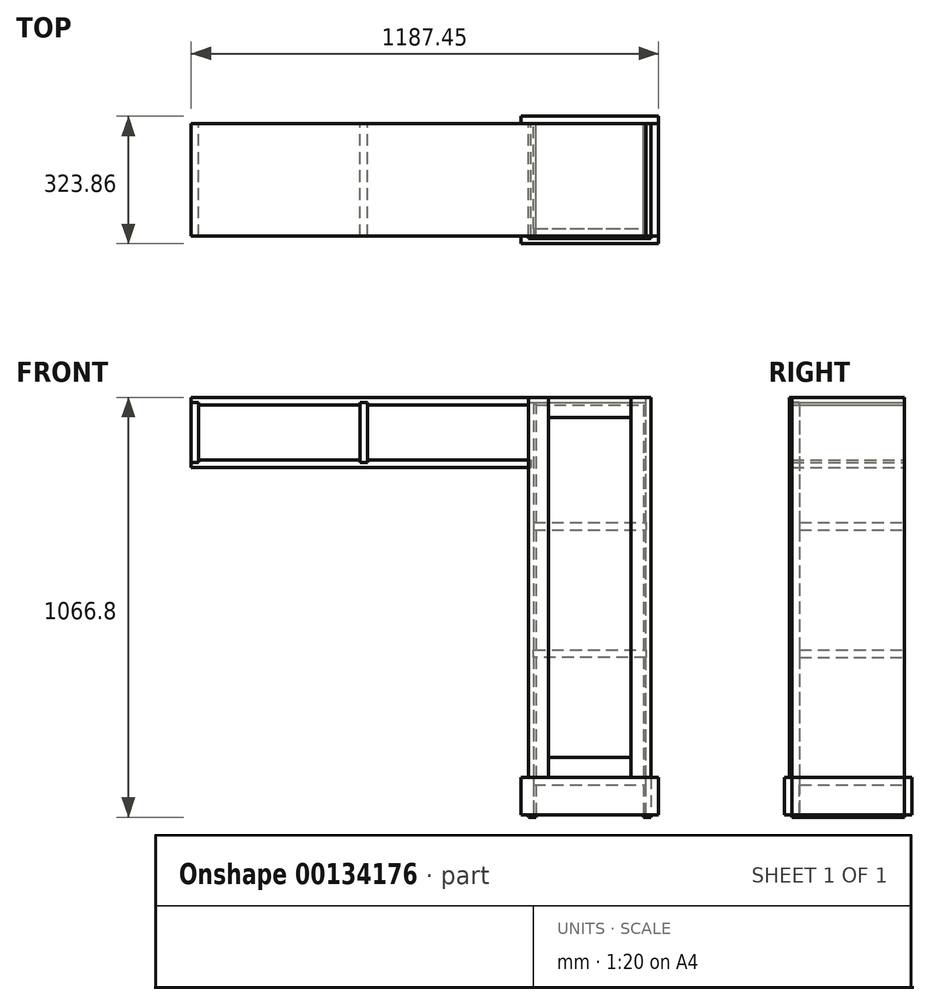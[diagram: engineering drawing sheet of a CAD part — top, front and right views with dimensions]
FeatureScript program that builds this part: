
annotation { "Feature Type Name" : "Feature", "Feature Type Description" : "" }
export const myFeature = defineFeature(function(context is Context, id is Id, definition is map)
    precondition{}
    {
        {
            var Q0;
            Q0=qCreatedBy(makeId("Front.planeOp"),FACE);
            var sketch = newSketch(context, id + "F0", { "sketchPlane" : qUnion([Q0])});
            skLineSegment(sketch, "E0.left", {"start": v(0, 908.05) * mm, "end": v(0, 1047.75) * mm});
            skLineSegment(sketch, "E0.right", {"start": v(19.05, 908.05) * mm, "end": v(19.05, 1047.75) * mm});
            skLineSegment(sketch, "E1.top", {"start": v(0, 889) * mm, "end": v(857.25, 889) * mm});
            skLineSegment(sketch, "E1.left", {"start": v(0, 908.05) * mm, "end": v(0, 889) * mm});
            skLineSegment(sketch, "E2.top", {"start": v(0, 1066.8) * mm, "end": v(1168.4, 1066.8) * mm});
            skLineSegment(sketch, "E2.left", {"start": v(0, 1047.75) * mm, "end": v(0, 1066.8) * mm});
            skLineSegment(sketch, "E2.right", {"start": v(1168.4, 1047.75) * mm, "end": v(1168.4, 1066.8) * mm});
            skLineSegment(sketch, "E3.top", {"start": v(857.25, 0) * mm, "end": v(876.3, 0) * mm});
            skLineSegment(sketch, "E3.left", {"start": v(857.25, 1047.75) * mm, "end": v(857.25, 908.05) * mm});
            skLineSegment(sketch, "E3.right", {"start": v(876.3, 1047.75) * mm, "end": v(876.3, 749.3) * mm});
            skLineSegment(sketch, "E4.top", {"start": v(1168.4, 0) * mm, "end": v(1149.35, 0) * mm});
            skLineSegment(sketch, "E4.left", {"start": v(1168.4, 1047.75) * mm, "end": v(1168.4, 0) * mm});
            skLineSegment(sketch, "E4.right", {"start": v(1149.35, 1047.75) * mm, "end": v(1149.35, 749.3) * mm});
            skLineSegment(sketch, "E5.bottom", {"start": v(876.3, 425.45) * mm, "end": v(1149.35, 425.45) * mm});
            skLineSegment(sketch, "E5.top", {"start": v(876.3, 406.4) * mm, "end": v(1149.35, 406.4) * mm});
            skLineSegment(sketch, "E6.top", {"start": v(857.25, 101.6) * mm, "end": v(838.2, 101.6) * mm});
            skLineSegment(sketch, "E6.left", {"start": v(857.25, 6.35) * mm, "end": v(857.25, 101.6) * mm});
            skLineSegment(sketch, "E7.bottom", {"start": v(1168.4, 6.35) * mm, "end": v(1187.45, 6.35) * mm});
            skLineSegment(sketch, "E7.top", {"start": v(1168.4, 101.6) * mm, "end": v(1187.45, 101.6) * mm});
            skLineSegment(sketch, "E7.left", {"start": v(1168.4, 6.35) * mm, "end": v(1168.4, 101.6) * mm});
            skLineSegment(sketch, "E8.bottom", {"start": v(838.2, 101.6) * mm, "end": v(857.25, 101.6) * mm});
            skLineSegment(sketch, "E8.left", {"start": v(838.2, 101.6) * mm, "end": v(838.2, 6.35) * mm});
            skLineSegment(sketch, "E8.right", {"start": v(1187.45, 101.6) * mm, "end": v(1187.45, 6.35) * mm});
            skLineSegment(sketch, "E9.bottom", {"start": v(876.3, 749.3) * mm, "end": v(1149.35, 749.3) * mm});
            skLineSegment(sketch, "E9.top", {"start": v(869.95, 730.25) * mm, "end": v(1149.35, 730.25) * mm});
            skLineSegment(sketch, "E10.bottom", {"start": v(876.3, 101.6) * mm, "end": v(1149.35, 101.6) * mm});
            skLineSegment(sketch, "E10.top", {"start": v(876.3, 82.55) * mm, "end": v(1149.35, 82.55) * mm});
            skLineSegment(sketch, "E11.bottom", {"start": v(876.3, 749.3) * mm, "end": v(869.95, 749.3) * mm});
            skLineSegment(sketch, "E11.top", {"start": v(876.3, 730.25) * mm, "end": v(869.95, 730.25) * mm});
            skLineSegment(sketch, "E11.right", {"start": v(869.95, 749.3) * mm, "end": v(869.95, 730.25) * mm});
            skLineSegment(sketch, "E12.bottom", {"start": v(1149.35, 749.3) * mm, "end": v(1155.7, 749.3) * mm});
            skLineSegment(sketch, "E12.top", {"start": v(1149.35, 730.25) * mm, "end": v(1155.7, 730.25) * mm});
            skLineSegment(sketch, "E12.right", {"start": v(1155.7, 749.3) * mm, "end": v(1155.7, 730.25) * mm});
            skLineSegment(sketch, "E13.trimOffspring", {"start": v(1149.35, 730.25) * mm, "end": v(1149.35, 425.45) * mm});
            skLineSegment(sketch, "E14.trimOffspring", {"start": v(876.3, 730.25) * mm, "end": v(876.3, 425.45) * mm});
            skLineSegment(sketch, "E15.trimOffspring", {"start": v(19.05, 908.05) * mm, "end": v(428.63, 908.05) * mm});
            skLineSegment(sketch, "E16.trimOffspring", {"start": v(19.05, 1047.75) * mm, "end": v(428.63, 1047.75) * mm});
            skLineSegment(sketch, "E17", {"start": v(19.05, 901.7) * mm, "end": v(0, 901.7) * mm});
            skLineSegment(sketch, "E18", {"start": v(19.05, 1054.1) * mm, "end": v(0, 1054.1) * mm});
            skLineSegment(sketch, "E19", {"start": v(19.05, 1047.75) * mm, "end": v(19.05, 1054.1) * mm});
            skLineSegment(sketch, "E20", {"start": v(19.05, 901.7) * mm, "end": v(19.05, 908.05) * mm});
            skLineSegment(sketch, "E21", {"start": v(428.63, 1054.1) * mm, "end": v(447.68, 1054.1) * mm});
            skLineSegment(sketch, "E22", {"start": v(447.68, 1047.75) * mm, "end": v(447.68, 901.7) * mm});
            skLineSegment(sketch, "E23", {"start": v(447.68, 901.7) * mm, "end": v(428.63, 901.7) * mm});
            skLineSegment(sketch, "E24", {"start": v(428.63, 901.7) * mm, "end": v(428.63, 1054.1) * mm});
            skLineSegment(sketch, "E25.trimOffspring", {"start": v(447.68, 1047.75) * mm, "end": v(857.25, 1047.75) * mm});
            skLineSegment(sketch, "E26.trimOffspring", {"start": v(447.68, 908.05) * mm, "end": v(857.25, 908.05) * mm});
            skLineSegment(sketch, "E27", {"start": v(857.25, 1054.1) * mm, "end": v(876.3, 1054.1) * mm});
            skLineSegment(sketch, "E28", {"start": v(857.25, 1054.1) * mm, "end": v(857.25, 1047.75) * mm});
            skLineSegment(sketch, "E29", {"start": v(857.25, 908.05) * mm, "end": v(863.6, 908.05) * mm});
            skLineSegment(sketch, "E30", {"start": v(863.6, 908.05) * mm, "end": v(863.6, 889) * mm});
            skLineSegment(sketch, "E31", {"start": v(863.6, 889) * mm, "end": v(857.25, 889) * mm});
            skLineSegment(sketch, "E32", {"start": v(1149.35, 1047.75) * mm, "end": v(1155.7, 1047.75) * mm});
            skLineSegment(sketch, "E33", {"start": v(876.3, 406.4) * mm, "end": v(869.95, 406.4) * mm});
            skLineSegment(sketch, "E34", {"start": v(869.95, 406.4) * mm, "end": v(869.95, 425.45) * mm});
            skLineSegment(sketch, "E35", {"start": v(869.95, 425.45) * mm, "end": v(1155.7, 425.45) * mm});
            skLineSegment(sketch, "E36", {"start": v(1155.7, 425.45) * mm, "end": v(1155.7, 406.4) * mm});
            skLineSegment(sketch, "E37", {"start": v(1155.7, 406.4) * mm, "end": v(1149.35, 406.4) * mm});
            skLineSegment(sketch, "E38.trimOffspring", {"start": v(1149.35, 406.4) * mm, "end": v(1149.35, 101.6) * mm});
            skLineSegment(sketch, "E39.trimOffspring", {"start": v(876.3, 406.4) * mm, "end": v(876.3, 101.6) * mm});
            skLineSegment(sketch, "E40", {"start": v(1149.35, 82.55) * mm, "end": v(1155.7, 82.55) * mm});
            skLineSegment(sketch, "E41", {"start": v(1155.7, 82.55) * mm, "end": v(1155.7, 101.6) * mm});
            skLineSegment(sketch, "E42", {"start": v(1155.7, 101.6) * mm, "end": v(869.95, 101.6) * mm});
            skLineSegment(sketch, "E43", {"start": v(869.95, 101.6) * mm, "end": v(869.95, 82.55) * mm});
            skLineSegment(sketch, "E44", {"start": v(869.95, 82.55) * mm, "end": v(876.3, 82.55) * mm});
            skLineSegment(sketch, "E45.trimOffspring", {"start": v(876.3, 82.55) * mm, "end": v(876.3, 0) * mm});
            skLineSegment(sketch, "E46.trimOffspring", {"start": v(1149.35, 82.55) * mm, "end": v(1149.35, 0) * mm});
            skLineSegment(sketch, "E47.trimOffspring", {"start": v(857.25, 889) * mm, "end": v(857.25, 0) * mm});
            skLineSegment(sketch, "E48.trimOffspring", {"start": v(876.3, 1047.75) * mm, "end": v(1149.35, 1047.75) * mm});
            skLineSegment(sketch, "E49", {"start": v(876.3, 1047.75) * mm, "end": v(876.3, 1054.1) * mm});
            skLineSegment(sketch, "E50.trimOffspring", {"start": v(869.95, 101.6) * mm, "end": v(1155.7, 101.6) * mm});
            skLineSegment(sketch, "E51", {"start": v(1155.7, 1047.75) * mm, "end": v(1155.7, 1066.8) * mm});
            skLineSegment(sketch, "E52", {"start": v(838.2, 6.35) * mm, "end": v(857.25, 6.35) * mm});
            skLineSegment(sketch, "E53", {"start": v(876.3, 0) * mm, "end": v(1149.35, 0) * mm});
            skLineSegment(sketch, "E54", {"start": v(447.68, 1054.1) * mm, "end": v(447.68, 1047.75) * mm});
            skSolve(sketch);
        }
        {
            var Q0;
            {var subQ0=sQuery(id+"F0.wireOp",EDGE,"E8.bottom");Q0=makeQuery(id+"F0.imprint","IMPRINT",FACE,{"disambiguationData":[TD([[makeQuery(id+"F0.imprint","IMPRINT",EDGE,{"derivedFrom":subQ0}),-1.0]])]});}
            var Q1;
            Q1=makeQuery(id+"F0.imprint","IMPRINT",FACE,{"disambiguationData":[TD([[makeQuery(id+"F0.imprint","IMPRINT",EDGE,{"derivedFrom":sQuery(id+"F0.wireOp",EDGE,"E10.top")}),1.0]])]});
            var Q2;
            Q2=makeQuery(id+"F0.imprint","IMPRINT",FACE,{"disambiguationData":[TD([[makeQuery(id+"F0.imprint","IMPRINT",EDGE,{"derivedFrom":sQuery(id+"F0.wireOp",EDGE,"E7.bottom")}),1.0]])]});
            var Q3;
            Q3=makeQuery(id+"F0.imprint","IMPRINT",FACE,{"disambiguationData":[TD([[makeQuery(id+"F0.imprint","IMPRINT",EDGE,{"derivedFrom":sQuery(id+"F0.wireOp",EDGE,"E5.top")}),1.0]])]});
            var Q4;
            Q4=makeQuery(id+"F0.imprint","IMPRINT",FACE,{"disambiguationData":[TD([[makeQuery(id+"F0.imprint","IMPRINT",EDGE,{"derivedFrom":sQuery(id+"F0.wireOp",EDGE,"E9.bottom")}),-1.0]])]});
            var Q5;
            {var subQ6=sQuery(id+"F0.wireOp",EDGE,"E16.trimOffspring");Q5=makeQuery(id+"F0.imprint","IMPRINT",FACE,{"disambiguationData":[TD([[makeQuery(id+"F0.imprint","IMPRINT",EDGE,{"derivedFrom":subQ6}),1.0]])]});}
            var Q6;
            {var subQ4=sQuery(id+"F0.wireOp",EDGE,"E1.top");Q6=makeQuery(id+"F0.imprint","IMPRINT",FACE,{"disambiguationData":[TD([[makeQuery(id+"F0.imprint","IMPRINT",EDGE,{"derivedFrom":subQ4}),1.0]])]});}
            extrude(context, id + "F1", {"entities" : qUnion([Q0, Q1, Q2, Q3, Q4, Q5, Q6]), "endBound" : BoundingType.SYMMETRIC, "depth" : 285.75 * mm});
        }
        {
            var Q0;
            {var subQ9=sQuery(id+"F0.wireOp",EDGE,"E3.top");Q0=makeQuery(id+"F0.imprint","IMPRINT",FACE,{"disambiguationData":[TD([[makeQuery(id+"F0.imprint","IMPRINT",EDGE,{"derivedFrom":subQ9}),1.0]])]});}
            var Q1;
            {var subQ1=sQuery(id+"F0.wireOp",EDGE,"E2.right");Q1=makeQuery(id+"F0.imprint","IMPRINT",FACE,{"disambiguationData":[TD([[makeQuery(id+"F0.imprint","IMPRINT",EDGE,{"derivedFrom":subQ1}),1.0]])]});}
            var Q2;
            {var subQ4=sQuery(id+"F0.wireOp",EDGE,"E21");Q2=makeQuery(id+"F0.imprint","IMPRINT",FACE,{"disambiguationData":[TD([[makeQuery(id+"F0.imprint","IMPRINT",EDGE,{"derivedFrom":subQ4}),-1.0]])]});}
            var Q3;
            {var subQ1=sQuery(id+"F0.wireOp",EDGE,"E0.left");Q3=makeQuery(id+"F0.imprint","IMPRINT",FACE,{"disambiguationData":[TD([[makeQuery(id+"F0.imprint","IMPRINT",EDGE,{"derivedFrom":subQ1}),-1.0]])]});}
            var Q4;
            Q4=makeQuery(id+"F1.opExtrude","CAP_FACE",FACE,{"disambiguationData":[OSD([sQuery(id+"F0.wireOp",EDGE,"E2.top"),sQuery(id+"F0.wireOp",EDGE,"E2.left"),sQuery(id+"F0.wireOp",EDGE,"E16.trimOffspring"),sQuery(id+"F0.wireOp",EDGE,"E18"),sQuery(id+"F0.wireOp",EDGE,"E19"),sQuery(id+"F0.wireOp",EDGE,"E21"),sQuery(id+"F0.wireOp",EDGE,"E24"),sQuery(id+"F0.wireOp",EDGE,"E25.trimOffspring"),sQuery(id+"F0.wireOp",EDGE,"E27"),sQuery(id+"F0.wireOp",EDGE,"E28"),sQuery(id+"F0.wireOp",EDGE,"E32"),sQuery(id+"F0.wireOp",EDGE,"E48.trimOffspring"),sQuery(id+"F0.wireOp",EDGE,"E49"),sQuery(id+"F0.wireOp",EDGE,"E51"),sQuery(id+"F0.wireOp",EDGE,"E54")])],"isStart":false});
            var Q5;
            Q5=makeQuery(id+"F1.opExtrude","CAP_FACE",FACE,{"disambiguationData":[OSD([sQuery(id+"F0.wireOp",EDGE,"E2.top"),sQuery(id+"F0.wireOp",EDGE,"E2.left"),sQuery(id+"F0.wireOp",EDGE,"E16.trimOffspring"),sQuery(id+"F0.wireOp",EDGE,"E18"),sQuery(id+"F0.wireOp",EDGE,"E19"),sQuery(id+"F0.wireOp",EDGE,"E21"),sQuery(id+"F0.wireOp",EDGE,"E24"),sQuery(id+"F0.wireOp",EDGE,"E25.trimOffspring"),sQuery(id+"F0.wireOp",EDGE,"E27"),sQuery(id+"F0.wireOp",EDGE,"E28"),sQuery(id+"F0.wireOp",EDGE,"E32"),sQuery(id+"F0.wireOp",EDGE,"E48.trimOffspring"),sQuery(id+"F0.wireOp",EDGE,"E49"),sQuery(id+"F0.wireOp",EDGE,"E51"),sQuery(id+"F0.wireOp",EDGE,"E54")])],"isStart":true});
            extrude(context, id + "F2", {"entities" : qUnion([Q0, Q1, Q2, Q3]), "endBound" : BoundingType.UP_TO_SURFACE, "endBoundEntityFace" : qUnion([Q4]), "depth" : 25.4 * mm, "hasSecondDirection" : true, "secondDirectionBound" : SecondDirectionBoundingType.UP_TO_SURFACE, "secondDirectionOppositeDirection" : true, "secondDirectionBoundEntityFace" : qUnion([Q5]), "secondDirectionDepth" : 25.4 * mm});
        }
        {
            var Q0;
            Q0=makeQuery(id+"F1.opExtrude","CAP_FACE",FACE,{"disambiguationData":[OSD([sQuery(id+"F0.wireOp",EDGE,"E2.top"),sQuery(id+"F0.wireOp",EDGE,"E2.left"),sQuery(id+"F0.wireOp",EDGE,"E16.trimOffspring"),sQuery(id+"F0.wireOp",EDGE,"E18"),sQuery(id+"F0.wireOp",EDGE,"E19"),sQuery(id+"F0.wireOp",EDGE,"E21"),sQuery(id+"F0.wireOp",EDGE,"E24"),sQuery(id+"F0.wireOp",EDGE,"E25.trimOffspring"),sQuery(id+"F0.wireOp",EDGE,"E27"),sQuery(id+"F0.wireOp",EDGE,"E28"),sQuery(id+"F0.wireOp",EDGE,"E32"),sQuery(id+"F0.wireOp",EDGE,"E48.trimOffspring"),sQuery(id+"F0.wireOp",EDGE,"E49"),sQuery(id+"F0.wireOp",EDGE,"E51"),sQuery(id+"F0.wireOp",EDGE,"E54")])],"isStart":false});
            var sketch = newSketch(context, id + "F3", { "sketchPlane" : qUnion([Q0])});
            skLineSegment(sketch, "E55.bottom", {"start": v(838.2, 101.6) * mm, "end": v(1187.45, 101.6) * mm});
            skLineSegment(sketch, "E55.top", {"start": v(838.2, 6.35) * mm, "end": v(1187.45, 6.35) * mm});
            skLineSegment(sketch, "E55.left", {"start": v(838.2, 101.6) * mm, "end": v(838.2, 6.35) * mm});
            skLineSegment(sketch, "E55.right", {"start": v(1187.45, 101.6) * mm, "end": v(1187.45, 6.35) * mm});
            skSolve(sketch);
        }
        {
            var Q0;
            Q0 = qSketchRegion(id + "F3", true);
            extrude(context, id + "F4", {"entities" : qUnion([Q0]), "depth" : 19.05 * mm});
        }
        {
            var Q0;
            Q0=makeQuery(id+"F1.opExtrude","CAP_FACE",FACE,{"disambiguationData":[OSD([sQuery(id+"F0.wireOp",EDGE,"E2.top"),sQuery(id+"F0.wireOp",EDGE,"E2.left"),sQuery(id+"F0.wireOp",EDGE,"E16.trimOffspring"),sQuery(id+"F0.wireOp",EDGE,"E18"),sQuery(id+"F0.wireOp",EDGE,"E19"),sQuery(id+"F0.wireOp",EDGE,"E21"),sQuery(id+"F0.wireOp",EDGE,"E24"),sQuery(id+"F0.wireOp",EDGE,"E25.trimOffspring"),sQuery(id+"F0.wireOp",EDGE,"E27"),sQuery(id+"F0.wireOp",EDGE,"E28"),sQuery(id+"F0.wireOp",EDGE,"E32"),sQuery(id+"F0.wireOp",EDGE,"E48.trimOffspring"),sQuery(id+"F0.wireOp",EDGE,"E49"),sQuery(id+"F0.wireOp",EDGE,"E51"),sQuery(id+"F0.wireOp",EDGE,"E54")])],"isStart":true});
            var sketch = newSketch(context, id + "F5", { "sketchPlane" : qUnion([Q0])});
            skLineSegment(sketch, "E56.bottom", {"start": v(-838.2, 101.6) * mm, "end": v(-838.2, 101.6) * mm});
            skLineSegment(sketch, "E56.top", {"start": v(-838.2, 101.6) * mm, "end": v(-838.2, 101.6) * mm});
            skLineSegment(sketch, "E56.left", {"start": v(-838.2, 101.6) * mm, "end": v(-838.2, 101.6) * mm});
            skLineSegment(sketch, "E56.right", {"start": v(-838.2, 101.6) * mm, "end": v(-838.2, 101.6) * mm});
            skLineSegment(sketch, "E57.bottom", {"start": v(-838.2, 101.6) * mm, "end": v(-1187.45, 101.6) * mm});
            skLineSegment(sketch, "E57.top", {"start": v(-838.2, 6.35) * mm, "end": v(-1187.45, 6.35) * mm});
            skLineSegment(sketch, "E57.left", {"start": v(-838.2, 101.6) * mm, "end": v(-838.2, 6.35) * mm});
            skLineSegment(sketch, "E57.right", {"start": v(-1187.45, 101.6) * mm, "end": v(-1187.45, 6.35) * mm});
            skSolve(sketch);
        }
        {
            var Q0;
            Q0 = qSketchRegion(id + "F5", true);
            extrude(context, id + "F6", {"entities" : qUnion([Q0]), "depth" : 19.05 * mm});
        }
        {
            var Q0;
            Q0=makeQuery(id+"F2.opExtrude","SWEPT_FACE",FACE,{"disambiguationData":[OSD([sQuery(id+"F0.wireOp",EDGE,"E2.top")])]});
            var sketch = newSketch(context, id + "F7", { "sketchPlane" : qUnion([Q0])});
            skLineSegment(sketch, "E58.bottom", {"start": v(0, 190.5) * mm, "end": v(1155.7, 190.5) * mm});
            skLineSegment(sketch, "E58.top", {"start": v(63.5, -190.5) * mm, "end": v(1155.7, -190.5) * mm});
            skLineSegment(sketch, "E58.left", {"start": v(0, 190.5) * mm, "end": v(0, -127) * mm});
            skLineSegment(sketch, "E58.right", {"start": v(1219.2, 127) * mm, "end": v(1219.2, -127) * mm});
            skPoint(sketch, "E59.visualSharp", {"position": v(1219.2, 190.5) * mm});
            skArc(sketch, "E59.filletArc", {"start": v(1219.2, 127) * mm, "mid": v(1200.6, 171.9) * mm, "end": v(1155.7, 190.5) * mm});
            skPoint(sketch, "E60.visualSharp", {"position": v(1219.2, -190.5) * mm});
            skArc(sketch, "E60.filletArc", {"start": v(1155.7, -190.5) * mm, "mid": v(1200.6, -171.9) * mm, "end": v(1219.2, -127) * mm});
            skPoint(sketch, "E61.visualSharp", {"position": v(0, -190.5) * mm});
            skArc(sketch, "E61.filletArc", {"start": v(0, -127) * mm, "mid": v(18.6, -171.9) * mm, "end": v(63.5, -190.5) * mm});
            skSolve(sketch);
        }
        {
            var Q0;
            Q0=makeQuery(id+"F1.opExtrude","CAP_FACE",FACE,{"disambiguationData":[OSD([sQuery(id+"F0.wireOp",EDGE,"E2.top"),sQuery(id+"F0.wireOp",EDGE,"E2.left"),sQuery(id+"F0.wireOp",EDGE,"E16.trimOffspring"),sQuery(id+"F0.wireOp",EDGE,"E18"),sQuery(id+"F0.wireOp",EDGE,"E19"),sQuery(id+"F0.wireOp",EDGE,"E21"),sQuery(id+"F0.wireOp",EDGE,"E24"),sQuery(id+"F0.wireOp",EDGE,"E25.trimOffspring"),sQuery(id+"F0.wireOp",EDGE,"E27"),sQuery(id+"F0.wireOp",EDGE,"E28"),sQuery(id+"F0.wireOp",EDGE,"E32"),sQuery(id+"F0.wireOp",EDGE,"E48.trimOffspring"),sQuery(id+"F0.wireOp",EDGE,"E49"),sQuery(id+"F0.wireOp",EDGE,"E51"),sQuery(id+"F0.wireOp",EDGE,"E54")])],"isStart":false});
            var sketch = newSketch(context, id + "F8", { "sketchPlane" : qUnion([Q0])});
            skLineSegment(sketch, "E62.bottom", {"start": v(869.95, 1054.1) * mm, "end": v(1155.7, 1054.1) * mm});
            skLineSegment(sketch, "E62.top", {"start": v(869.95, 6.35) * mm, "end": v(1155.7, 6.35) * mm});
            skLineSegment(sketch, "E62.left", {"start": v(869.95, 1054.1) * mm, "end": v(869.95, 6.35) * mm});
            skLineSegment(sketch, "E62.right", {"start": v(1155.7, 1054.1) * mm, "end": v(1155.7, 6.35) * mm});
            skSolve(sketch);
        }
        {
            var Q0;
            Q0 = qSketchRegion(id + "F8", true);
            extrude(context, id + "F9", {"entities" : qUnion([Q0]), "operationType" : NewBodyOperationType.REMOVE, "oppositeDirection" : true, "depth" : 19.05 * mm});
        }
        {
            var Q0;
            Q0 = qSketchRegion(id + "F8", true);
            extrude(context, id + "F10", {"entities" : qUnion([Q0]), "oppositeDirection" : true, "depth" : 19.05 * mm});
        }
        {
            var Q0;
            Q0=makeQuery(id+"F1.opExtrude","CAP_FACE",FACE,{"disambiguationData":[OSD([sQuery(id+"F0.wireOp",EDGE,"E2.top"),sQuery(id+"F0.wireOp",EDGE,"E2.left"),sQuery(id+"F0.wireOp",EDGE,"E16.trimOffspring"),sQuery(id+"F0.wireOp",EDGE,"E18"),sQuery(id+"F0.wireOp",EDGE,"E19"),sQuery(id+"F0.wireOp",EDGE,"E21"),sQuery(id+"F0.wireOp",EDGE,"E24"),sQuery(id+"F0.wireOp",EDGE,"E25.trimOffspring"),sQuery(id+"F0.wireOp",EDGE,"E27"),sQuery(id+"F0.wireOp",EDGE,"E28"),sQuery(id+"F0.wireOp",EDGE,"E32"),sQuery(id+"F0.wireOp",EDGE,"E48.trimOffspring"),sQuery(id+"F0.wireOp",EDGE,"E49"),sQuery(id+"F0.wireOp",EDGE,"E51"),sQuery(id+"F0.wireOp",EDGE,"E54")])],"isStart":false});
            var sketch = newSketch(context, id + "F11", { "sketchPlane" : qUnion([Q0])});
            skLineSegment(sketch, "E63.bottom", {"start": v(857.25, 1066.8) * mm, "end": v(908.05, 1066.8) * mm});
            skLineSegment(sketch, "E63.top", {"start": v(857.25, 101.6) * mm, "end": v(908.05, 101.6) * mm});
            skLineSegment(sketch, "E63.left", {"start": v(857.25, 1066.8) * mm, "end": v(857.25, 101.6) * mm});
            skLineSegment(sketch, "E63.right", {"start": v(908.05, 1066.8) * mm, "end": v(908.05, 101.6) * mm});
            skLineSegment(sketch, "E64.bottom", {"start": v(1168.4, 1066.8) * mm, "end": v(1117.6, 1066.8) * mm});
            skLineSegment(sketch, "E64.top", {"start": v(1168.4, 101.6) * mm, "end": v(1117.6, 101.6) * mm});
            skLineSegment(sketch, "E64.left", {"start": v(1168.4, 1066.8) * mm, "end": v(1168.4, 101.6) * mm});
            skLineSegment(sketch, "E64.right", {"start": v(1117.6, 1066.8) * mm, "end": v(1117.6, 101.6) * mm});
            skLineSegment(sketch, "E65.bottom", {"start": v(908.05, 1066.8) * mm, "end": v(1117.6, 1066.8) * mm});
            skLineSegment(sketch, "E65.top", {"start": v(908.05, 1016) * mm, "end": v(908.05, 1016) * mm});
            skLineSegment(sketch, "E65.left", {"start": v(908.05, 1066.8) * mm, "end": v(908.05, 1016) * mm});
            skLineSegment(sketch, "E65.right", {"start": v(1117.6, 1066.8) * mm, "end": v(1117.6, 1016) * mm});
            skLineSegment(sketch, "E66.bottom", {"start": v(908.05, 101.6) * mm, "end": v(1117.6, 101.6) * mm});
            skLineSegment(sketch, "E66.top", {"start": v(908.05, 152.4) * mm, "end": v(908.05, 152.4) * mm});
            skLineSegment(sketch, "E66.left", {"start": v(908.05, 101.6) * mm, "end": v(908.05, 152.4) * mm});
            skLineSegment(sketch, "E66.right", {"start": v(1117.6, 101.6) * mm, "end": v(1117.6, 152.4) * mm});
            skLineSegment(sketch, "E67", {"start": v(1117.6, 152.4) * mm, "end": v(1117.6, 152.4) * mm});
            skLineSegment(sketch, "E68", {"start": v(908.05, 152.4) * mm, "end": v(1117.6, 152.4) * mm});
            skLineSegment(sketch, "E69", {"start": v(908.05, 1016) * mm, "end": v(1117.6, 1016) * mm});
            skLineSegment(sketch, "E70", {"start": v(1117.6, 1016) * mm, "end": v(1117.6, 1016) * mm});
            skSolve(sketch);
        }
        {
            var Q0;
            Q0=makeQuery(id+"F11.imprint","IMPRINT",FACE,{"disambiguationData":[TD([[makeQuery(id+"F11.imprint","IMPRINT",EDGE,{"derivedFrom":sQuery(id+"F11.wireOp",EDGE,"E66.bottom")}),1.0]])]});
            var Q1;
            {var subQ0=sQuery(id+"F11.wireOp",EDGE,"E65.bottom");Q1=makeQuery(id+"F11.imprint","IMPRINT",FACE,{"disambiguationData":[TD([[makeQuery(id+"F11.imprint","IMPRINT",EDGE,{"derivedFrom":subQ0}),-1.0]])]});}
            var Q2;
            {var subQ0=sQuery(id+"F11.wireOp",EDGE,"E69");Q2=makeQuery(id+"F11.imprint","IMPRINT",FACE,{"disambiguationData":[TD([[makeQuery(id+"F11.imprint","IMPRINT",EDGE,{"derivedFrom":subQ0}),1.0]])]});}
            extrude(context, id + "F12", {"entities" : qUnion([Q0, Q1, Q2]), "depth" : 6.35 * mm});
        }
        {
            var Q0;
            Q0=makeQuery(id+"F11.imprint","IMPRINT",FACE,{"disambiguationData":[TD([[makeQuery(id+"F11.imprint","IMPRINT",EDGE,{"derivedFrom":sQuery(id+"F11.wireOp",EDGE,"E63.bottom")}),-1.0]])]});
            var Q1;
            Q1=makeQuery(id+"F11.imprint","IMPRINT",FACE,{"disambiguationData":[TD([[makeQuery(id+"F11.imprint","IMPRINT",EDGE,{"derivedFrom":sQuery(id+"F11.wireOp",EDGE,"E64.bottom")}),-1.0]])]});
            var Q2;
            {var subQ7=sQuery(id+"F11.wireOp",EDGE,"E63.top");Q2=makeQuery(id+"F11.imprint","IMPRINT",FACE,{"disambiguationData":[TD([[makeQuery(id+"F11.imprint","IMPRINT",EDGE,{"derivedFrom":subQ7}),1.0]])]});}
            var Q3;
            Q3=makeQuery(id+"F11.imprint","IMPRINT",FACE,{"disambiguationData":[TD([[makeQuery(id+"F11.imprint","IMPRINT",EDGE,{"derivedFrom":sQuery(id+"F11.wireOp",EDGE,"E64.top")}),-1.0]])]});
            var Q4;
            Q4=makeQuery(id+"F12.opExtrude","CAP_FACE",FACE,{"disambiguationData":[OSD([sQuery(id+"F11.wireOp",EDGE,"E66.bottom"),sQuery(id+"F11.wireOp",EDGE,"E66.left"),sQuery(id+"F11.wireOp",EDGE,"E66.right"),sQuery(id+"F11.wireOp",EDGE,"E68")])],"isStart":false});
            extrude(context, id + "F13", {"entities" : qUnion([Q0, Q1, Q2, Q3]), "endBound" : BoundingType.UP_TO_SURFACE, "endBoundEntityFace" : qUnion([Q4]), "depth" : 25.4 * mm});
        }
    });
